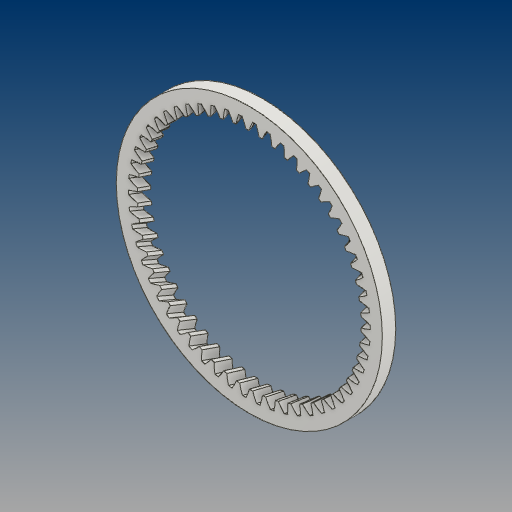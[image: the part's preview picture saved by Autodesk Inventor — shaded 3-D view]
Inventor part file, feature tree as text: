
AUTODESK INVENTOR PART (.ipt)
format: ipt  version: 2021 (Build 250183000, 183)  size: 780,288 bytes
history: native  units: mm (DEFAULTED — no unit token found)
features: plane x3, other x3, sketch x2, extrude x1
ambient origin geometry x8: Origin, YZ Plane, XZ Plane, XY Plane, X Axis, Y Axis, Z Axis, Center Point
bodies: Solid1 (feature_tree)
feature tree (9):
  extrude  "Extrusion1"  Depth=15.0mm TaperAngle=0.0deg
  plane  "Work Plane2"
  plane  "Work Plane8"
  plane  "Work Plane9"
  other  "Spur Gear"
  sketch  "Sketch1"  dims[d0=297.614736mm d1=15.0mm d2=0.0mm]
  sketch  "Sketch2"  dims[d3=258.595199mm d4=10.0mm d5=0.0mm d16=65.0mm d17=0.0mm d34=0.581776mm d39=0.0mm d45=0.0mm d47=65.0mm d50=0.0mm d51=0.0mm d52=65.0mm]
  other  "Srf1"
  other  "Pitch Diameter"
